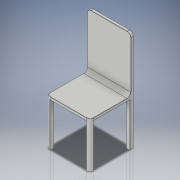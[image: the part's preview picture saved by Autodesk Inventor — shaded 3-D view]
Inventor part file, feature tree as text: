
AUTODESK INVENTOR PART (.ipt)
format: ipt  version: 2018 (Build 220112000, 112)  size: 211,456 bytes
history: native  units: in
note: dims shown in document units (in); Inventor stores cm internally (conversion verified against a paired STEP export)
features: extrude x3, fillet x3, sketch x3
ambient origin geometry x8: Origin, YZ Plane, XZ Plane, XY Plane, X Axis, Y Axis, Z Axis, Center Point
bodies: Solid1 (feature_tree)
feature tree (9):
  extrude  "Extrusion1"  Depth=24.0in
  extrude  "Extrusion2"  Depth=1.5in
  extrude  "Extrusion3"  Depth=2.0in
  fillet  "Fillet1"  Radius=2.0in
  fillet  "Fillet3"  Radius=2.0in
  fillet  "Fillet2"  Radius=2.0in
  sketch  "Sketch1"  dims[d0=24.0in d1=24.0in]
  sketch  "Sketch2"  dims[d2=1.5in d3=0.0in d4=1.5in]
  sketch  "Sketch3"  dims[d5=30.0in d6=0.0in d7=2.0in d8=2.0in d9=2.0in d10=2.0in d11=2.0in d12=2.0in d14=2.0in d15=2.0in d16=24.0in d17=0.0in d18=2.0in d19=0.125in d20=2.0in]
